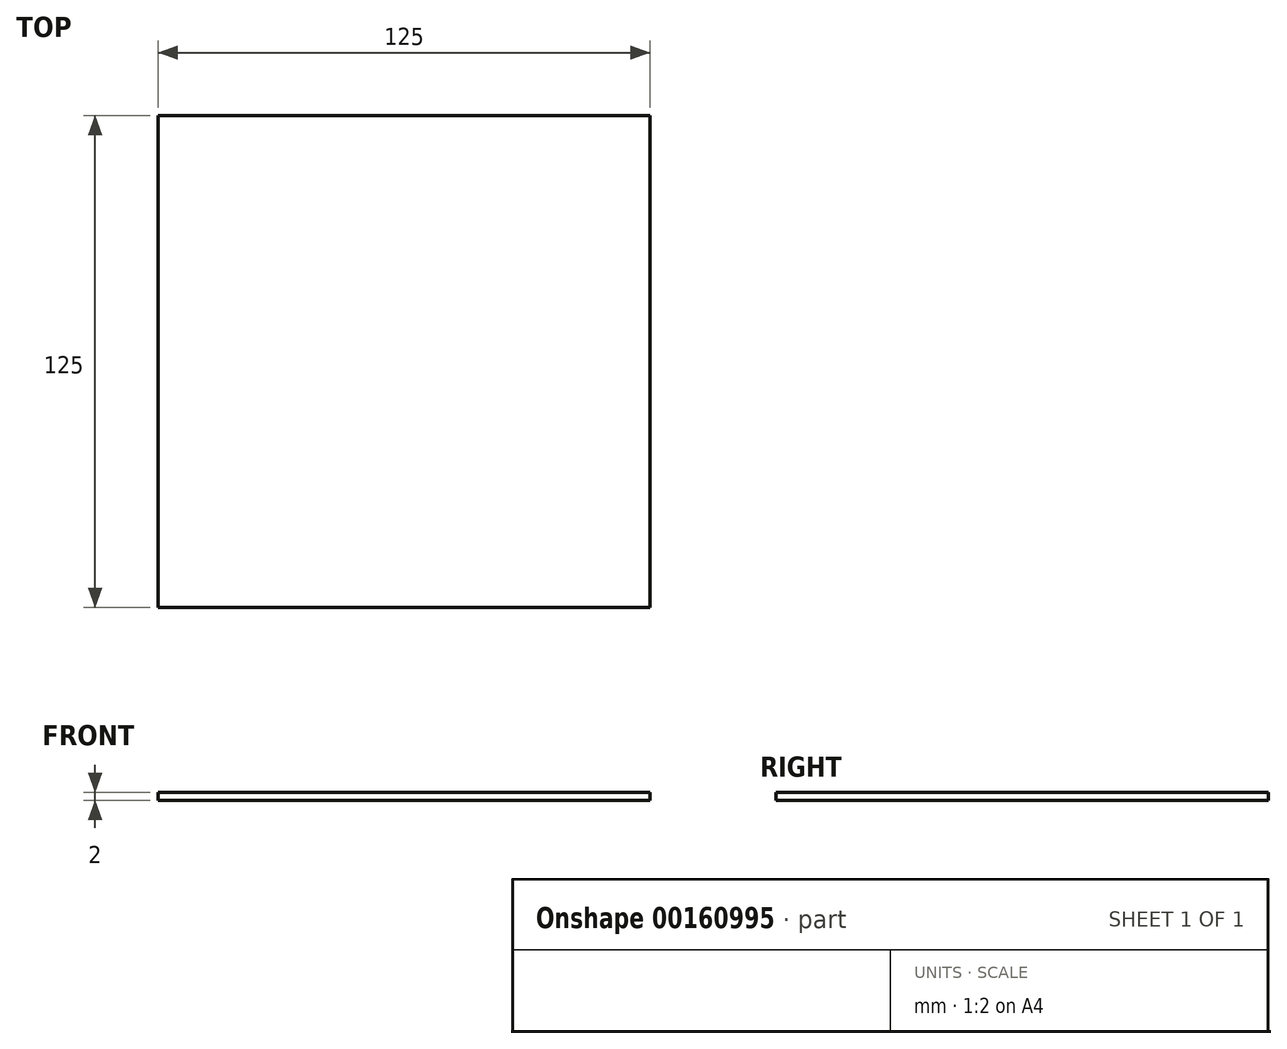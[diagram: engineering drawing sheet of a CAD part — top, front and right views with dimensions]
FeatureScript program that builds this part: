
annotation { "Feature Type Name" : "Feature", "Feature Type Description" : "" }
export const myFeature = defineFeature(function(context is Context, id is Id, definition is map)
    precondition{}
    {
        {
            var Q0;
            Q0=qCreatedBy(makeId("Top.planeOp"),FACE);
            var sketch = newSketch(context, id + "F0", { "sketchPlane" : qUnion([Q0])});
            skLineSegment(sketch, "E0.bottom", {"start": v(-62.41, 61.57) * mm, "end": v(62.59, 61.57) * mm});
            skLineSegment(sketch, "E0.top", {"start": v(-62.41, -63.43) * mm, "end": v(62.59, -63.43) * mm});
            skLineSegment(sketch, "E0.left", {"start": v(-62.41, 61.57) * mm, "end": v(-62.41, -63.43) * mm});
            skLineSegment(sketch, "E0.right", {"start": v(62.59, 61.57) * mm, "end": v(62.59, -63.43) * mm});
            skSolve(sketch);
        }
        {
            var Q0;
            Q0=makeQuery(id+"F0.imprint","IMPRINT",FACE,{"disambiguationData":[TD([[makeQuery(id+"F0.imprint","IMPRINT",EDGE,{"derivedFrom":sQuery(id+"F0.wireOp",EDGE,"E0.bottom")}),-1.0]])]});
            extrude(context, id + "F1", {"entities" : qUnion([Q0]), "depth" : 2 * mm});
        }
    });
